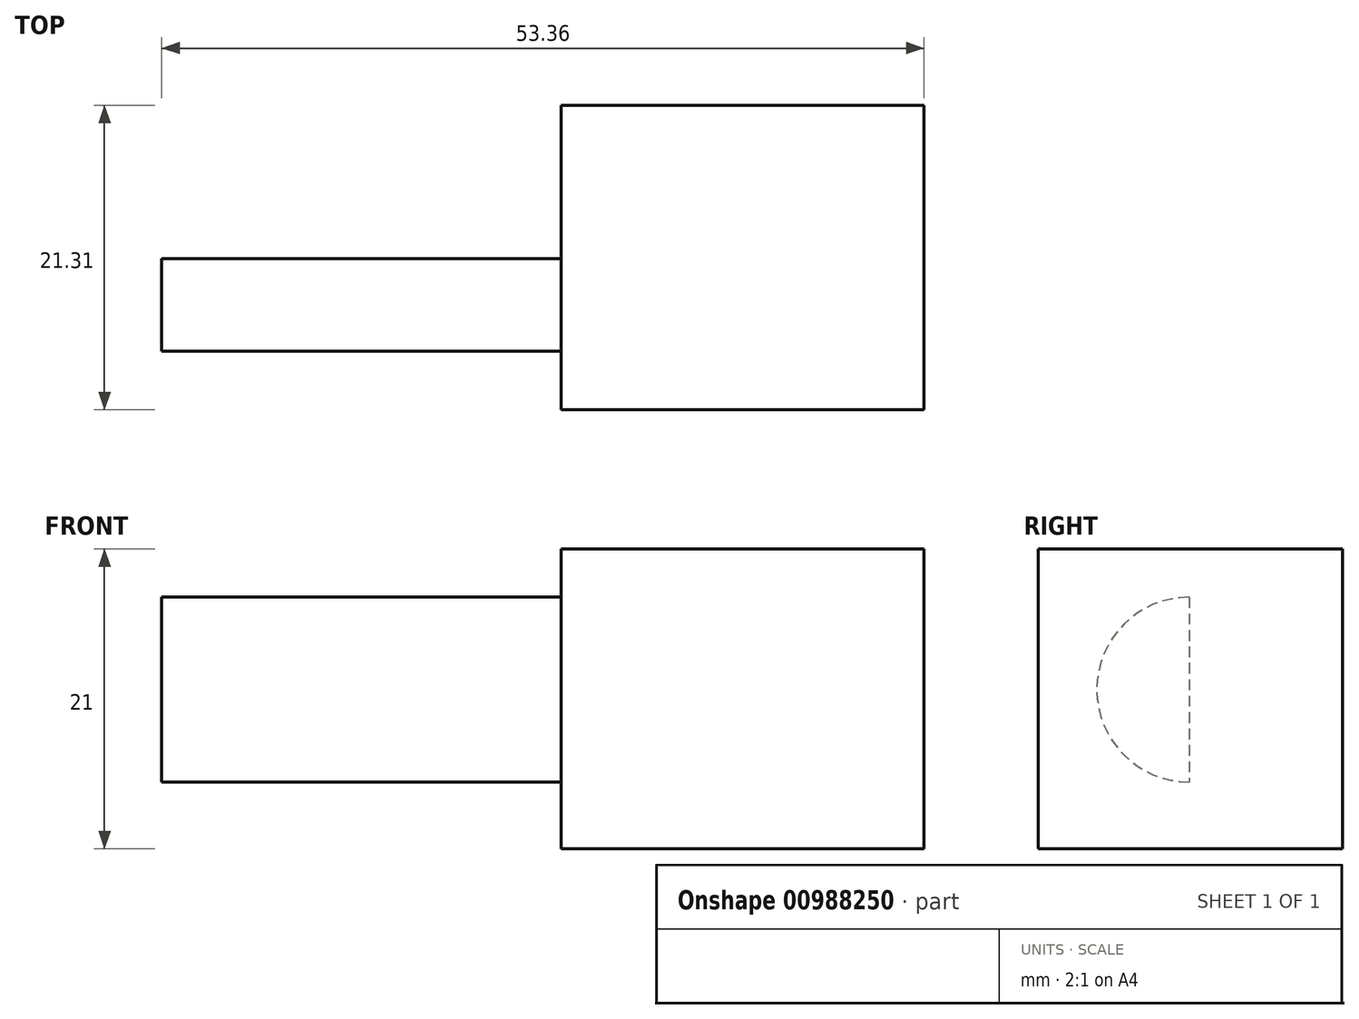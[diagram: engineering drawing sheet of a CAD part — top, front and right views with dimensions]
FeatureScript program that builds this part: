
annotation { "Feature Type Name" : "Feature", "Feature Type Description" : "" }
export const myFeature = defineFeature(function(context is Context, id is Id, definition is map)
    precondition{}
    {
        {
            var Q0;
            Q0=qCreatedBy(makeId("Right.planeOp"),FACE);
            var sketch = newSketch(context, id + "F0", { "sketchPlane" : qUnion([Q0])});
            skLineSegment(sketch, "E0.bottom", {"start": v(-21.3, 21) * mm, "end": v(0, 21) * mm});
            skLineSegment(sketch, "E0.top", {"start": v(-21.3, 0) * mm, "end": v(0, 0) * mm});
            skLineSegment(sketch, "E0.left", {"start": v(-21.3, 21) * mm, "end": v(-21.3, 0) * mm});
            skLineSegment(sketch, "E0.right", {"start": v(0, 21) * mm, "end": v(0, 0) * mm});
            skSolve(sketch);
        }
        {
            var Q0;
            Q0 = qSketchRegion(id + "F0", true);
            extrude(context, id + "F1", {"entities" : qUnion([Q0]), "depth" : 25.4 * mm, "offsetDistance" : 25.4 * mm});
        }
        {
            var Q0;
            Q0=makeQuery(id+"F1.opExtrude","CAP_FACE",FACE,{"disambiguationData":[OSD([sQuery(id+"F0.wireOp",EDGE,"E0.bottom"),sQuery(id+"F0.wireOp",EDGE,"E0.top"),sQuery(id+"F0.wireOp",EDGE,"E0.left"),sQuery(id+"F0.wireOp",EDGE,"E0.right")])],"isStart":false});
            var sketch = newSketch(context, id + "F2", { "sketchPlane" : qUnion([Q0])});
            skCircle(sketch, "E1", {"center": v(-10.74, 11.15) * mm, "radius": 6.47 * mm});
            skLineSegment(sketch, "E2", {"start": v(-10.75, 23.46) * mm, "end": v(-10.75, -3.5) * mm});
            skSolve(sketch);
        }
        {
            var Q0;
            {var subQ0=sQuery(id+"F2.wireOp",EDGE,"E2");var subQ1=sQuery(id+"F2.wireOp",EDGE,"E1");var subQ2=makeQuery(id+"F2.imprint","INTERSECT",VERTEX,{"disambiguationData":[OD(0.0)],"derivedFrom":[subQ1,subQ0]});Q0=makeQuery(id+"F2.imprint","IMPRINT",FACE,{"disambiguationData":[TD([[makeQuery(id+"F2.imprint","IMPRINT",EDGE,{"disambiguationData":[TD([[subQ2,-1.0]])],"derivedFrom":subQ1}),1.0]])]});}
            extrude(context, id + "F3", {"entities" : qUnion([Q0]), "operationType" : NewBodyOperationType.ADD, "oppositeDirection" : true, "depth" : 53.36 * mm, "offsetDistance" : 25.4 * mm});
        }
    });
